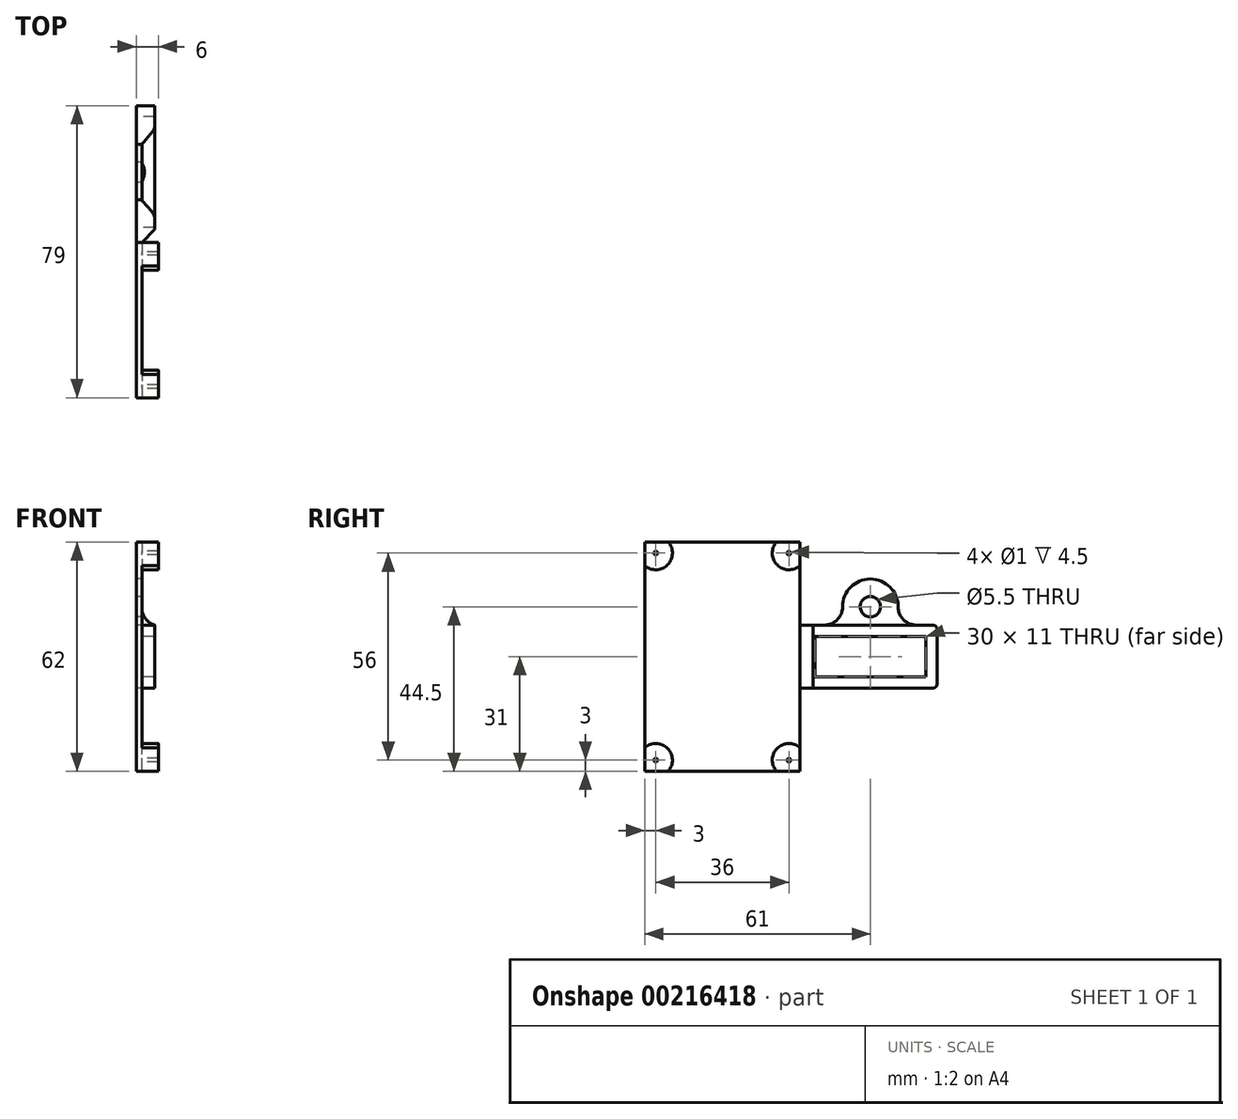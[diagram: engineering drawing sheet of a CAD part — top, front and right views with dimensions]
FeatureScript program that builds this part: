
annotation { "Feature Type Name" : "Feature", "Feature Type Description" : "" }
export const myFeature = defineFeature(function(context is Context, id is Id, definition is map)
    precondition{}
    {
        {
            var Q0;
            Q0=qCreatedBy(makeId("Right.planeOp"),FACE);
            var sketch = newSketch(context, id + "F0", { "sketchPlane" : qUnion([Q0])});
            skLineSegment(sketch, "E0.bottom", {"start": v(-15, 5.5) * mm, "end": v(15, 5.5) * mm});
            skLineSegment(sketch, "E0.top", {"start": v(-15, -5.5) * mm, "end": v(15, -5.5) * mm});
            skLineSegment(sketch, "E0.left", {"start": v(-15, 5.5) * mm, "end": v(-15, -5.5) * mm});
            skLineSegment(sketch, "E0.right", {"start": v(15, 5.5) * mm, "end": v(15, -5.5) * mm});
            skCircle(sketch, "E1", {"center": v(0, 13.5) * mm, "radius": 2.75 * mm});
            skLineSegment(sketch, "E2.bottom", {"start": v(-17.8, 8.5) * mm, "end": v(-12.5, 8.5) * mm, "construction": true});
            skLineSegment(sketch, "E2.top", {"start": v(-14.13, -8.5) * mm, "end": v(18, -8.5) * mm, "construction": true});
            skLineSegment(sketch, "E2.right", {"start": v(18, 8.5) * mm, "end": v(18, -8.5) * mm});
            skCircle(sketch, "E3", {"center": v(0, 13.5) * mm, "radius": 7.5 * mm, "construction": true});
            skLineSegment(sketch, "E4", {"start": v(-7.5, 13.5) * mm, "end": v(-7.5, 13.5) * mm});
            skLineSegment(sketch, "E5", {"start": v(7.5, 13.5) * mm, "end": v(7.5, 13.5) * mm});
            skArc(sketch, "E6", {"start": v(7.5, 13.5) * mm, "mid": v(0, 21) * mm, "end": v(-7.5, 13.5) * mm});
            skArc(sketch, "E7.filletArc", {"start": v(-12.5, 8.5) * mm, "mid": v(-8.96, 9.96) * mm, "end": v(-7.5, 13.5) * mm});
            skLineSegment(sketch, "E8", {"start": v(12.5, 8.5) * mm, "end": v(18, 8.5) * mm});
            skPoint(sketch, "E9.visualSharp", {"position": v(7.5, 8.5) * mm});
            skArc(sketch, "E9.filletArc", {"start": v(7.5, 13.5) * mm, "mid": v(8.96, 9.96) * mm, "end": v(12.5, 8.5) * mm});
            skLineSegment(sketch, "E10.bottom", {"start": v(-60, 30) * mm, "end": v(-20, 30) * mm, "construction": true});
            skLineSegment(sketch, "E10.top", {"start": v(-60, -30) * mm, "end": v(-20, -30) * mm, "construction": true});
            skLineSegment(sketch, "E10.left", {"start": v(-60, 30) * mm, "end": v(-60, -30) * mm, "construction": true});
            skLineSegment(sketch, "E10.right", {"start": v(-20, 30) * mm, "end": v(-20, -30) * mm, "construction": true});
            skLineSegment(sketch, "E11.bottom", {"start": v(-61, 31) * mm, "end": v(-19, 31) * mm});
            skLineSegment(sketch, "E11.top", {"start": v(-61, -31) * mm, "end": v(-19, -31) * mm});
            skLineSegment(sketch, "E11.left", {"start": v(-61, 31) * mm, "end": v(-61, -31) * mm});
            skLineSegment(sketch, "E11.right", {"start": v(-19, 31) * mm, "end": v(-19, -31) * mm, "construction": true});
            skLineSegment(sketch, "E12", {"start": v(-12.5, 8.5) * mm, "end": v(-19, 8.5) * mm});
            skLineSegment(sketch, "E13", {"start": v(18, -8.5) * mm, "end": v(-19, -8.5) * mm});
            skLineSegment(sketch, "E14", {"start": v(-19, 31) * mm, "end": v(-19, 8.5) * mm, "construction": true});
            skLineSegment(sketch, "E15", {"start": v(-19, 31) * mm, "end": v(-19, 8.5) * mm});
            skLineSegment(sketch, "E16", {"start": v(-19, -8.5) * mm, "end": v(-19, -31) * mm});
            skLineSegment(sketch, "E17", {"start": v(-40, 0) * mm, "end": v(-40, 49.07) * mm, "construction": true});
            skSolve(sketch);
        }
        {
            var Q0;
            Q0=makeQuery(id+"F0.imprint","IMPRINT",FACE,{"disambiguationData":[TD([[makeQuery(id+"F0.imprint","IMPRINT",EDGE,{"derivedFrom":sQuery(id+"F0.wireOp",EDGE,"E0.bottom")}),1.0]])]});
            extrude(context, id + "F1", {"entities" : qUnion([Q0]), "depth" : 1.5 * mm});
        }
        {
            var Q0;
            Q0=qCreatedBy(makeId("Right.planeOp"),FACE);
            var sketch = newSketch(context, id + "F2", { "sketchPlane" : qUnion([Q0])});
            skLineSegment(sketch, "E18.bottom", {"start": v(-15, 5.5) * mm, "end": v(15, 5.5) * mm});
            skLineSegment(sketch, "E18.top", {"start": v(-15, -5.5) * mm, "end": v(15, -5.5) * mm});
            skLineSegment(sketch, "E18.left", {"start": v(-15, 5.5) * mm, "end": v(-15, -5.5) * mm});
            skLineSegment(sketch, "E18.right", {"start": v(15, 5.5) * mm, "end": v(15, -5.5) * mm});
            skLineSegment(sketch, "E19.bottom", {"start": v(-19, 8.5) * mm, "end": v(18, 8.5) * mm});
            skLineSegment(sketch, "E19.top", {"start": v(-19, -8.5) * mm, "end": v(18, -8.5) * mm});
            skLineSegment(sketch, "E19.left", {"start": v(-19, 8.5) * mm, "end": v(-19, -8.5) * mm});
            skLineSegment(sketch, "E19.right", {"start": v(18, 8.5) * mm, "end": v(18, -8.5) * mm});
            skSolve(sketch);
        }
        {
            var Q0;
            Q0 = qSketchRegion(id + "F2", true);
            extrude(context, id + "F3", {"entities" : qUnion([Q0]), "operationType" : NewBodyOperationType.ADD, "depth" : 5 * mm});
        }
        {
            var Q0;
            Q0=makeQuery(id+"F3.boolean.opBoolean","INTERSECT",EDGE,{"derivedFrom":[makeQuery(id+"F1.opExtrude","CAP_FACE",FACE,{"disambiguationData":[OSD([sQuery(id+"F0.wireOp",EDGE,"E0.bottom"),sQuery(id+"F0.wireOp",EDGE,"E0.top"),sQuery(id+"F0.wireOp",EDGE,"E0.left"),sQuery(id+"F0.wireOp",EDGE,"E0.right"),sQuery(id+"F0.wireOp",EDGE,"E1"),sQuery(id+"F0.wireOp",EDGE,"E2.right"),sQuery(id+"F0.wireOp",EDGE,"E6"),sQuery(id+"F0.wireOp",EDGE,"E7.filletArc"),sQuery(id+"F0.wireOp",EDGE,"E8"),sQuery(id+"F0.wireOp",EDGE,"E9.filletArc"),sQuery(id+"F0.wireOp",EDGE,"412b617e-81df-4353-afdc-f88c2fd28d67"),sQuery(id+"F0.wireOp",EDGE,"E11.bottom"),sQuery(id+"F0.wireOp",EDGE,"E11.top"),sQuery(id+"F0.wireOp",EDGE,"E11.left"),sQuery(id+"F0.wireOp",EDGE,"E12"),sQuery(id+"F0.wireOp",EDGE,"E13"),sQuery(id+"F0.wireOp",EDGE,"E15"),sQuery(id+"F0.wireOp",EDGE,"E16"),sQuery(id+"F0.wireOp",EDGE,"914caccd-d7ac-43ed-bfab-883ccd15350e0.MirrorC"),sQuery(id+"F0.wireOp",EDGE,"8bfd3fed-4d00-4387-93dd-7852bc2b0d700.MirrorC"),sQuery(id+"F0.wireOp",EDGE,"92ec00c3-27d1-4d62-b9e9-8c0948b770a20.MirrorC")])],"isStart":false}),makeQuery(id+"F3.opExtrude","SWEPT_FACE",FACE,{"disambiguationData":[OSD([sQuery(id+"F2.wireOp",EDGE,"E19.bottom")])]})]});
            fillet(context, id + "F4", {"entities" : qUnion([Q0]), "radius" : 5 * mm, "tangentPropagation" : true, "allowEdgeOverflow" : false});
        }
        {
            var Q0;
            Q0=makeQuery(id+"F3.opExtrude","CAP_EDGE",EDGE,{"disambiguationData":[OSD([sQuery(id+"F2.wireOp",EDGE,"E19.left")])],"isStart":false});
            chamfer(context, id + "F5", {"entities" : qUnion([Q0]), "width" : 3.5 * mm, "tangentPropagation" : true});
        }
        {
            var Q0;
            Q0=makeQuery(id+"F3.boolean.opBoolean","MERGE",EDGE,{"derivedFrom":[makeQuery(id+"F1.opExtrude","SWEPT_EDGE",EDGE,{"disambiguationData":[OSD([sQuery(id+"F0.wireOp",EDGE,"E2.right"),sQuery(id+"F0.wireOp",EDGE,"E8")])]}),makeQuery(id+"F3.opExtrude","SWEPT_EDGE",EDGE,{"disambiguationData":[OSD([sQuery(id+"F2.wireOp",EDGE,"E19.bottom"),sQuery(id+"F2.wireOp",EDGE,"E19.right")])]})]});
            var Q1;
            Q1=makeQuery(id+"F3.boolean.opBoolean","MERGE",EDGE,{"derivedFrom":[makeQuery(id+"F1.opExtrude","SWEPT_EDGE",EDGE,{"disambiguationData":[OSD([sQuery(id+"F0.wireOp",EDGE,"E2.right"),sQuery(id+"F0.wireOp",EDGE,"E13")])]}),makeQuery(id+"F3.opExtrude","SWEPT_EDGE",EDGE,{"disambiguationData":[OSD([sQuery(id+"F2.wireOp",EDGE,"E19.top"),sQuery(id+"F2.wireOp",EDGE,"E19.right")])]})]});
            fillet(context, id + "F6", {"entities" : qUnion([Q0, Q1]), "radius" : 1 * mm, "tangentPropagation" : true, "allowEdgeOverflow" : false});
        }
        {
            var Q0;
            Q0=qCreatedBy(makeId("Right.planeOp"),FACE);
            var sketch = newSketch(context, id + "F7", { "sketchPlane" : qUnion([Q0])});
            skLineSegment(sketch, "E20.bottom", {"start": v(-60, 30) * mm, "end": v(-20, 30) * mm, "construction": true});
            skLineSegment(sketch, "E20.top", {"start": v(-60, -30) * mm, "end": v(-20, -30) * mm, "construction": true});
            skLineSegment(sketch, "E20.left", {"start": v(-60, 30) * mm, "end": v(-60, -30) * mm, "construction": true});
            skLineSegment(sketch, "E20.right", {"start": v(-20, 30) * mm, "end": v(-20, -30) * mm, "construction": true});
            skLineSegment(sketch, "E21.bottom", {"start": v(-61, 31) * mm, "end": v(-19, 31) * mm, "construction": true});
            skLineSegment(sketch, "E21.top", {"start": v(-61, -31) * mm, "end": v(-19, -31) * mm, "construction": true});
            skLineSegment(sketch, "E21.left", {"start": v(-61, 31) * mm, "end": v(-61, -31) * mm, "construction": true});
            skLineSegment(sketch, "E22", {"start": v(-40, 0) * mm, "end": v(-40, 49.07) * mm, "construction": true});
            skCircle(sketch, "E23", {"center": v(-58, 28) * mm, "radius": 1 * mm, "construction": true});
            skCircle(sketch, "E24", {"center": v(-58, 28) * mm, "radius": 4.5 * mm, "construction": true});
            skArc(sketch, "E25", {"start": v(-61, 24.65) * mm, "mid": v(-54.82, 24.82) * mm, "end": v(-54.65, 31) * mm});
            skArc(sketch, "E26.MirrorCS", {"start": v(-19, 24.65) * mm, "mid": v(-25.18, 24.82) * mm, "end": v(-25.35, 31) * mm});
            skArc(sketch, "E27.MirrorCS", {"start": v(-19, -24.65) * mm, "mid": v(-25.18, -24.82) * mm, "end": v(-25.35, -31) * mm});
            skArc(sketch, "E28.MirrorCS", {"start": v(-61, -24.65) * mm, "mid": v(-54.82, -24.82) * mm, "end": v(-54.65, -31) * mm});
            skCircle(sketch, "E29", {"center": v(-58, 28) * mm, "radius": 0.5 * mm});
            skCircle(sketch, "E30.MirrorC", {"center": v(-22, 28) * mm, "radius": 0.5 * mm});
            skCircle(sketch, "E31.MirrorC", {"center": v(-58, -28) * mm, "radius": 0.5 * mm});
            skCircle(sketch, "E32.MirrorC", {"center": v(-22, -28) * mm, "radius": 0.5 * mm});
            skLineSegment(sketch, "E33", {"start": v(-61, -24.65) * mm, "end": v(-61, -31) * mm});
            skLineSegment(sketch, "E34", {"start": v(-54.65, -31) * mm, "end": v(-61, -31) * mm});
            skLineSegment(sketch, "E35", {"start": v(-25.35, -31) * mm, "end": v(-19, -31) * mm});
            skLineSegment(sketch, "E36", {"start": v(-19, -31) * mm, "end": v(-19, -24.65) * mm});
            skLineSegment(sketch, "E37", {"start": v(-19, 24.65) * mm, "end": v(-19, 31) * mm});
            skLineSegment(sketch, "E38", {"start": v(-25.35, 31) * mm, "end": v(-19, 31) * mm});
            skLineSegment(sketch, "E39", {"start": v(-54.65, 31) * mm, "end": v(-61, 31) * mm});
            skLineSegment(sketch, "E40", {"start": v(-61, 24.65) * mm, "end": v(-61, 31) * mm});
            skSolve(sketch);
        }
        {
            var Q0;
            Q0 = qSketchRegion(id + "F7", true);
            extrude(context, id + "F8", {"entities" : qUnion([Q0]), "operationType" : NewBodyOperationType.ADD, "depth" : 6 * mm});
        }
    });
